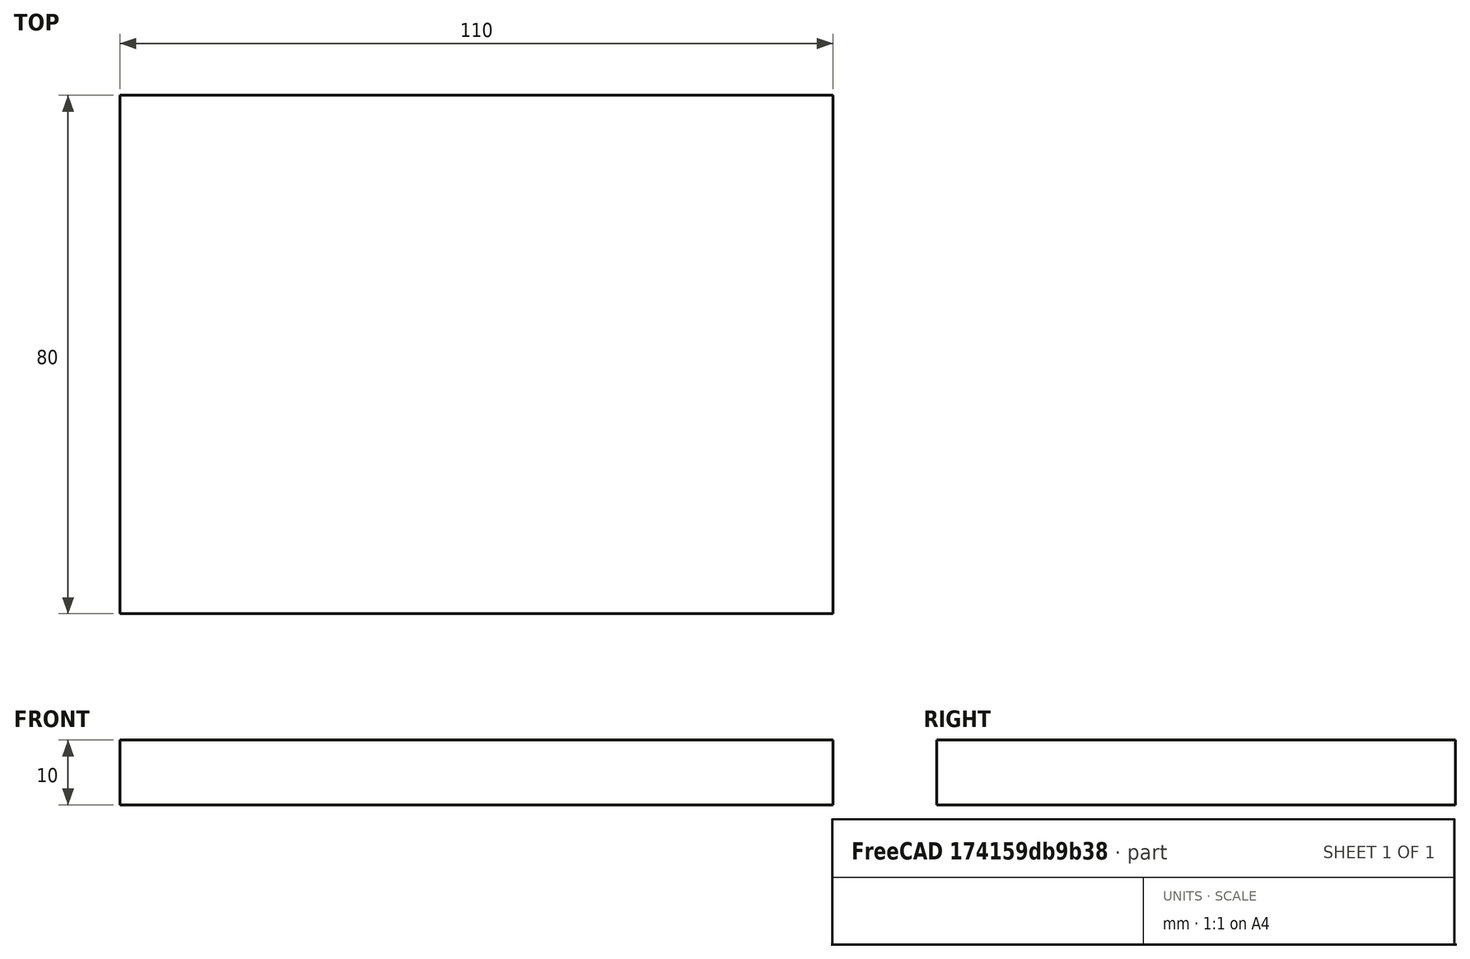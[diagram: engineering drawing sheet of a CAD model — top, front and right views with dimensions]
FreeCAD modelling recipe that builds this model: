
FCSTD DOCUMENT  (FreeCAD 0.18R4 (GitTag))
Label: Divider-E
License: All rights reserved
LicenseURL: http://en.wikipedia.org/wiki/All_rights_reserved
objects: Sketcher::SketchObject×1, PartDesign::Pad×1, PartDesign::Body×1
note: 4 computed .brp shape members not serialized (recipe doc carries the construction recipe); baked Part::Feature solids carry a one-line shape summary decoded from their .brp

FEATURE [Sketcher::SketchObject] Sketch
  MapMode = 5
  Support = -> [XY_Plane]
  sketch-geometry (4):
    g0: LineSegment StartX=0 StartY=0 StartZ=0 EndX=-110 EndY=0 EndZ=0
    g1: LineSegment StartX=-110 StartY=0 StartZ=0 EndX=-110 EndY=80 EndZ=0
    g2: LineSegment StartX=-110 StartY=80 StartZ=0 EndX=0 EndY=80 EndZ=0
    g3: LineSegment StartX=0 StartY=80 StartZ=0 EndX=0 EndY=0 EndZ=0
  constraints (11):
    c: Coincident(g0,g1)
    c: Coincident(g1,g2)
    c: Coincident(g2,g3)
    c: Coincident(g3,g0)
    c: Horizontal(g0)
    c: Horizontal(g2)
    c: Vertical(g1)
    c: Vertical(g3)
    c: Distance(g2) = 110
    c: Distance(g3) = 80
    c: Coincident(g0,g-1)
FEATURE [PartDesign::Pad] Pad
  Length = 10
  Length2 = 100
  Profile = -> Sketch
  Type = 0
FEATURE [PartDesign::Body] Body
  Group = -> [Sketch,Pad]
  Origin = -> Origin
  Tip = -> Pad
